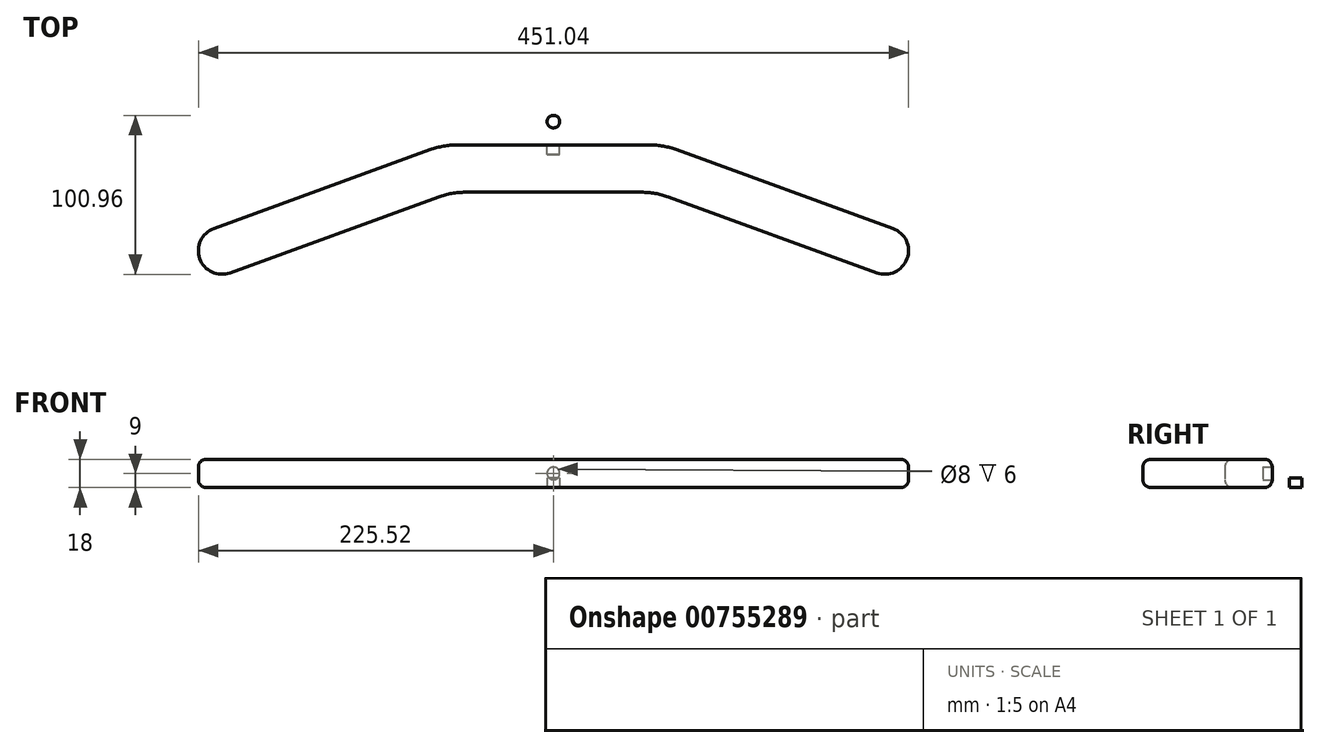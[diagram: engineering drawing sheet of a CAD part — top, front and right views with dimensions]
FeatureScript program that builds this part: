
annotation { "Feature Type Name" : "Feature", "Feature Type Description" : "" }
export const myFeature = defineFeature(function(context is Context, id is Id, definition is map)
    precondition{}
    {
        {
            var Q0;
            Q0=qCreatedBy(makeId("Top.planeOp"),FACE);
            var sketch = newSketch(context, id + "F0", { "sketchPlane" : qUnion([Q0])});
            skLineSegment(sketch, "E0", {"start": v(0, 0) * mm, "end": v(-61.18, 0) * mm});
            skLineSegment(sketch, "E1", {"start": v(-78.28, -3.02) * mm, "end": v(-215.65, -53.01) * mm});
            skLineSegment(sketch, "E2", {"start": v(-224.62, -72.24) * mm, "end": v(-224.62, -72.24) * mm});
            skLineSegment(sketch, "E3", {"start": v(-205.4, -81.2) * mm, "end": v(-73, -33.02) * mm});
            skLineSegment(sketch, "E4", {"start": v(-55.9, -30) * mm, "end": v(0, -30) * mm});
            skPoint(sketch, "E5.visualSharp", {"position": v(-70, 0) * mm});
            skArc(sketch, "E5.filletArc", {"start": v(-61.18, 0) * mm, "mid": v(-69.87, -0.76) * mm, "end": v(-78.28, -3.02) * mm});
            skPoint(sketch, "E6.visualSharp", {"position": v(-64.71, -30) * mm});
            skArc(sketch, "E6.filletArc", {"start": v(-55.9, -30) * mm, "mid": v(-64.58, -30.76) * mm, "end": v(-73, -33.02) * mm});
            skPoint(sketch, "E7.visualSharp", {"position": v(-219.49, -86.33) * mm});
            skArc(sketch, "E7.filletArc", {"start": v(-224.62, -72.24) * mm, "mid": v(-216.86, -80.7) * mm, "end": v(-205.4, -81.2) * mm});
            skPoint(sketch, "E8.visualSharp", {"position": v(-229.75, -58.14) * mm});
            skArc(sketch, "E8.filletArc", {"start": v(-215.65, -53.01) * mm, "mid": v(-224.12, -60.77) * mm, "end": v(-224.62, -72.24) * mm});
            skLineSegment(sketch, "E9.MirrorCS", {"start": v(78.28, -3.02) * mm, "end": v(215.65, -53.01) * mm});
            skLineSegment(sketch, "E10.MirrorCS", {"start": v(205.4, -81.2) * mm, "end": v(73, -33.02) * mm});
            skLineSegment(sketch, "E11.MirrorCS", {"start": v(0, 0) * mm, "end": v(61.18, 0) * mm});
            skPoint(sketch, "E12.MirrorP", {"position": v(219.49, -86.33) * mm});
            skLineSegment(sketch, "E13.MirrorCS", {"start": v(55.9, -30) * mm, "end": v(0, -30) * mm});
            skPoint(sketch, "E14.MirrorP", {"position": v(229.75, -58.14) * mm});
            skArc(sketch, "E15.MirrorCS", {"start": v(61.18, 0) * mm, "mid": v(69.87, -0.76) * mm, "end": v(78.28, -3.02) * mm});
            skPoint(sketch, "E16.MirrorP", {"position": v(64.71, -30) * mm});
            skArc(sketch, "E17.MirrorCS", {"start": v(55.9, -30) * mm, "mid": v(64.58, -30.76) * mm, "end": v(73, -33.02) * mm});
            skArc(sketch, "E18.MirrorCS", {"start": v(224.62, -72.24) * mm, "mid": v(216.86, -80.7) * mm, "end": v(205.4, -81.2) * mm});
            skLineSegment(sketch, "E19.MirrorCS", {"start": v(224.62, -72.24) * mm, "end": v(224.62, -72.24) * mm});
            skPoint(sketch, "E20.MirrorP", {"position": v(70, 0) * mm});
            skArc(sketch, "E21.MirrorCS", {"start": v(215.65, -53.01) * mm, "mid": v(224.12, -60.77) * mm, "end": v(224.62, -72.24) * mm});
            skLineSegment(sketch, "E22", {"start": v(-225.52, -16.85) * mm, "end": v(-225.52, -113.46) * mm, "construction": true});
            skLineSegment(sketch, "E23", {"start": v(225.52, -25.7) * mm, "end": v(225.52, -126.18) * mm, "construction": true});
            skLineSegment(sketch, "E24", {"start": v(-255.89, -82.1) * mm, "end": v(-73.3, -82.1) * mm, "construction": true});
            skLineSegment(sketch, "E25", {"start": v(-70, 0) * mm, "end": v(-229.75, -58.14) * mm, "construction": true});
            skLineSegment(sketch, "E26", {"start": v(-64.71, -30) * mm, "end": v(-219.49, -86.33) * mm, "construction": true});
            skPoint(sketch, "E27", {"position": v(-225.52, -56.6) * mm});
            skPoint(sketch, "E28", {"position": v(-225.52, -82.1) * mm});
            skPoint(sketch, "E29", {"position": v(-207.88, -82.1) * mm});
            skPoint(sketch, "E30", {"position": v(-225.52, -67.1) * mm});
            skPoint(sketch, "E31", {"position": v(-210.52, -82.1) * mm});
            skLineSegment(sketch, "E32", {"start": v(-212.97, -83.96) * mm, "end": v(-225.52, -88.53) * mm, "construction": true});
            skSolve(sketch);
        }
        {
            var Q0;
            Q0 = qSketchRegion(id + "F0", true);
            extrude(context, id + "F1", {"entities" : qUnion([Q0]), "depth" : 18 * mm, "offsetDistance" : 25 * mm});
        }
        {
            var Q0;
            Q0=makeQuery(id+"F1.opExtrude","SWEPT_FACE",FACE,{"disambiguationData":[OSD([sQuery(id+"F0.wireOp",EDGE,"E0"),sQuery(id+"F0.wireOp",EDGE,"E11.MirrorCS")])]});
            var sketch = newSketch(context, id + "F2", { "sketchPlane" : qUnion([Q0])});
            skCircle(sketch, "E33", {"center": v(0, 9) * mm, "radius": 4 * mm});
            skSolve(sketch);
        }
        {
            var Q0;
            Q0 = qSketchRegion(id + "F2", true);
            extrude(context, id + "F3", {"entities" : qUnion([Q0]), "operationType" : NewBodyOperationType.REMOVE, "oppositeDirection" : true, "depth" : 6 * mm, "offsetDistance" : 25 * mm});
        }
        {
            var Q0;
            Q0=qCreatedBy(makeId("Top.planeOp"),FACE);
            var sketch = newSketch(context, id + "F4", { "sketchPlane" : qUnion([Q0])});
            skCircle(sketch, "E34", {"center": v(0, 14.85) * mm, "radius": 4 * mm});
            skSolve(sketch);
        }
        {
            var Q0;
            Q0 = qSketchRegion(id + "F4", true);
            extrude(context, id + "F5", {"entities" : qUnion([Q0]), "depth" : 6 * mm, "offsetDistance" : 25 * mm});
        }
        {
            var Q0;
            Q0=makeQuery(id+"F1.opExtrude","CAP_EDGE",EDGE,{"disambiguationData":[OSD([sQuery(id+"F0.wireOp",EDGE,"E0"),sQuery(id+"F0.wireOp",EDGE,"E11.MirrorCS")])],"isStart":true});
            var Q1;
            Q1=makeQuery(id+"F1.opExtrude","CAP_EDGE",EDGE,{"disambiguationData":[OSD([sQuery(id+"F0.wireOp",EDGE,"E0"),sQuery(id+"F0.wireOp",EDGE,"E11.MirrorCS")])],"isStart":false});
            fillet(context, id + "F6", {"entities" : qUnion([Q0, Q1]), "radius" : 5 * mm, "tangentPropagation" : true, "allowEdgeOverflow" : false});
        }
    });
